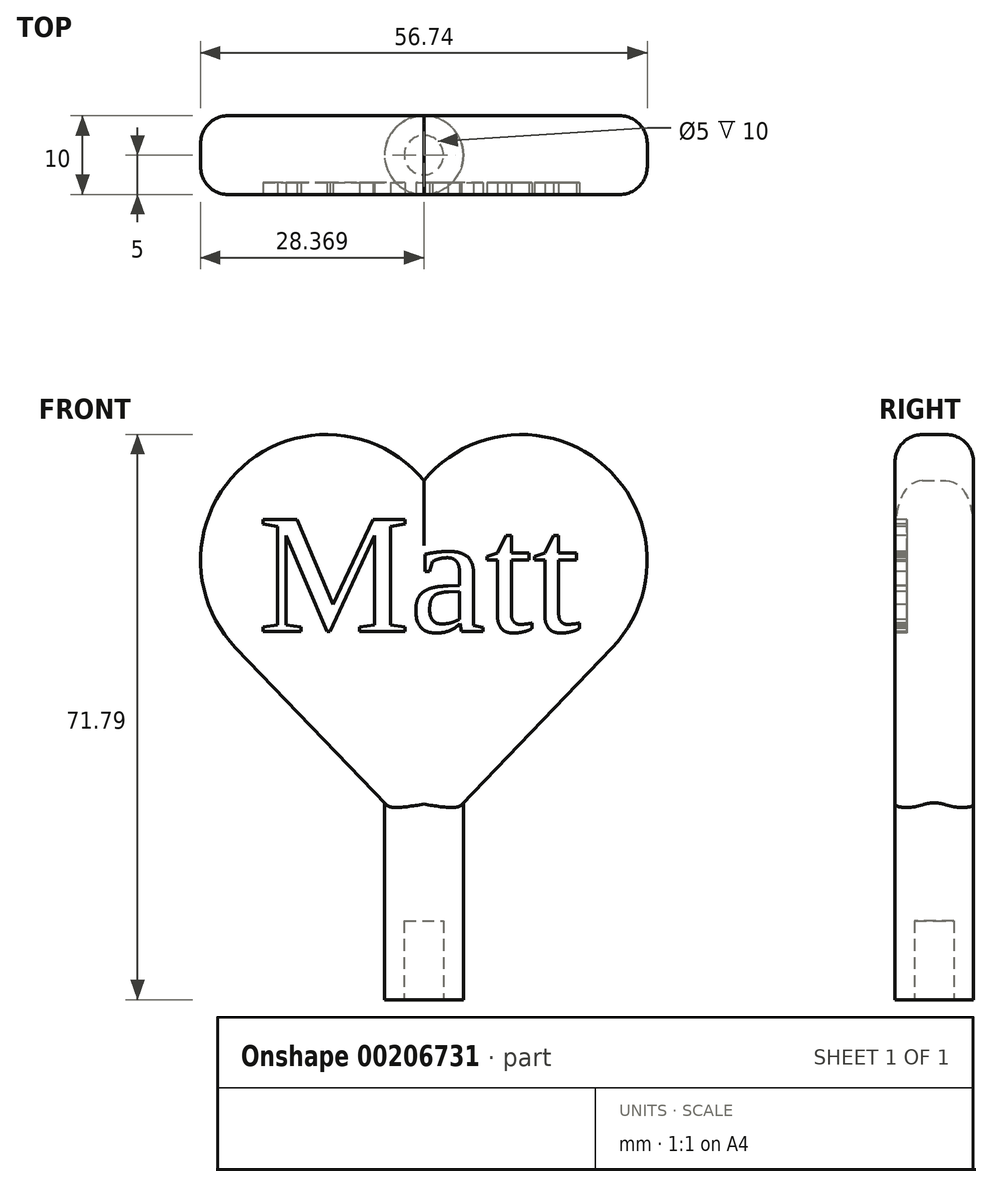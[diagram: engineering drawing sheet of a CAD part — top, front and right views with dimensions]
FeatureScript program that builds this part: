
annotation { "Feature Type Name" : "Feature", "Feature Type Description" : "" }
export const myFeature = defineFeature(function(context is Context, id is Id, definition is map)
    precondition{}
    {
        {
            var Q0;
            Q0=qCreatedBy(makeId("Front.planeOp"),FACE);
            var sketch = newSketch(context, id + "F0", { "sketchPlane" : qUnion([Q0])});
            skArc(sketch, "E0", {"start": v(-13.24, 54.95) * mm, "mid": v(-36.24, 56.75) * mm, "end": v(-37.15, 33.7) * mm});
            skArc(sketch, "E1.MirrorCS", {"start": v(-13.24, 54.95) * mm, "mid": v(9.76, 56.75) * mm, "end": v(10.67, 33.7) * mm});
            skLineSegment(sketch, "E2", {"start": v(-18.24, 14) * mm, "end": v(-8.24, 14) * mm});
            skLineSegment(sketch, "E3", {"start": v(-37.15, 33.7) * mm, "end": v(-18.24, 14) * mm});
            skLineSegment(sketch, "E4", {"start": v(10.67, 33.7) * mm, "end": v(-8.24, 14) * mm});
            skSolve(sketch);
        }
        {
            var Q0;
            Q0=makeQuery(id+"F0.imprint","IMPRINT",FACE,{"disambiguationData":[TD([[makeQuery(id+"F0.imprint","IMPRINT",EDGE,{"derivedFrom":sQuery(id+"F0.wireOp",EDGE,"E0")}),1.0]])]});
            extrude(context, id + "F1", {"entities" : qUnion([Q0]), "depth" : 10 * mm});
        }
        {
            var Q0;
            Q0=makeQuery(id+"F1.opExtrude","SWEPT_FACE",FACE,{"disambiguationData":[OSD([sQuery(id+"F0.wireOp",EDGE,"E2")])]});
            extrude(context, id + "F2", {"entities" : qUnion([Q0]), "operationType" : NewBodyOperationType.ADD, "depth" : 25 * mm});
        }
        {
            var Q0;
            Q0=makeQuery(id+"F1.opExtrude","CAP_EDGE",EDGE,{"disambiguationData":[OSD([sQuery(id+"F0.wireOp",EDGE,"E1.MirrorCS")])],"isStart":false});
            var Q1;
            Q1=makeQuery(id+"F1.opExtrude","CAP_EDGE",EDGE,{"disambiguationData":[OSD([sQuery(id+"F0.wireOp",EDGE,"E0")])],"isStart":false});
            var Q2;
            Q2=makeQuery(id+"F1.opExtrude","CAP_EDGE",EDGE,{"disambiguationData":[OSD([sQuery(id+"F0.wireOp",EDGE,"E3")])],"isStart":false});
            var Q3;
            Q3=makeQuery(id+"F1.opExtrude","CAP_EDGE",EDGE,{"disambiguationData":[OSD([sQuery(id+"F0.wireOp",EDGE,"E4")])],"isStart":false});
            var Q4;
            Q4=makeQuery(id+"F1.opExtrude","CAP_EDGE",EDGE,{"disambiguationData":[OSD([sQuery(id+"F0.wireOp",EDGE,"E4")])],"isStart":true});
            var Q5;
            Q5=makeQuery(id+"F1.opExtrude","CAP_EDGE",EDGE,{"disambiguationData":[OSD([sQuery(id+"F0.wireOp",EDGE,"E1.MirrorCS")])],"isStart":true});
            var Q6;
            Q6=makeQuery(id+"F1.opExtrude","CAP_EDGE",EDGE,{"disambiguationData":[OSD([sQuery(id+"F0.wireOp",EDGE,"E0")])],"isStart":true});
            var Q7;
            Q7=makeQuery(id+"F1.opExtrude","CAP_EDGE",EDGE,{"disambiguationData":[OSD([sQuery(id+"F0.wireOp",EDGE,"E3")])],"isStart":true});
            fillet(context, id + "F3", {"entities" : qUnion([Q0, Q1, Q2, Q3, Q4, Q5, Q6, Q7]), "radius" : 3.5 * mm, "tangentPropagation" : true, "allowEdgeOverflow" : false});
        }
        {
            var Q0;
            {var subQ0=sQuery(id+"F0.wireOp",EDGE,"E3");var subQ1=sQuery(id+"F0.wireOp",EDGE,"E2");Q0=makeQuery(id+"F2.opExtrude","SWEPT_EDGE",EDGE,{"disambiguationData":[OSD([subQ1,subQ0]),TDD([makeQuery(id+"F1.opExtrude","CAP_VERTEX",VERTEX,{"disambiguationData":[OSD([subQ1,subQ0])],"isStart":false})])]});}
            var Q1;
            {var subQ0=sQuery(id+"F0.wireOp",EDGE,"E4");var subQ1=sQuery(id+"F0.wireOp",EDGE,"E2");Q1=makeQuery(id+"F2.opExtrude","SWEPT_EDGE",EDGE,{"disambiguationData":[OSD([subQ1,subQ0]),TDD([makeQuery(id+"F1.opExtrude","CAP_VERTEX",VERTEX,{"disambiguationData":[OSD([subQ1,subQ0])],"isStart":false})])]});}
            var Q2;
            {var subQ0=sQuery(id+"F0.wireOp",EDGE,"E4");var subQ1=sQuery(id+"F0.wireOp",EDGE,"E2");Q2=makeQuery(id+"F2.opExtrude","SWEPT_EDGE",EDGE,{"disambiguationData":[OSD([subQ1,subQ0]),TDD([makeQuery(id+"F1.opExtrude","CAP_VERTEX",VERTEX,{"disambiguationData":[OSD([subQ1,subQ0])],"isStart":true})])]});}
            var Q3;
            {var subQ0=sQuery(id+"F0.wireOp",EDGE,"E3");var subQ1=sQuery(id+"F0.wireOp",EDGE,"E2");Q3=makeQuery(id+"F2.opExtrude","SWEPT_EDGE",EDGE,{"disambiguationData":[OSD([subQ1,subQ0]),TDD([makeQuery(id+"F1.opExtrude","CAP_VERTEX",VERTEX,{"disambiguationData":[OSD([subQ1,subQ0])],"isStart":true})])]});}
            fillet(context, id + "F4", {"entities" : qUnion([Q0, Q1, Q2, Q3]), "radius" : 5 * mm, "tangentPropagation" : true, "allowEdgeOverflow" : false});
        }
        {
            var Q0;
            Q0=makeQuery(id+"F2.opExtrude","CAP_FACE",FACE,{"disambiguationData":[OSD([sQuery(id+"F0.wireOp",EDGE,"E2")])],"isStart":false});
            var sketch = newSketch(context, id + "F5", { "sketchPlane" : qUnion([Q0])});
            skCircle(sketch, "E5", {"center": v(-13.24, 5) * mm, "radius": 2.5 * mm});
            skSolve(sketch);
        }
        {
            var Q0;
            {var subQ0=sQuery(id+"F0.wireOp",EDGE,"E2");Q0=makeQuery(id+"F2.boolean.opBoolean","MERGE",FACE,{"derivedFrom":[makeQuery(id+"F1.opExtrude","CAP_FACE",FACE,{"disambiguationData":[OSD([sQuery(id+"F0.wireOp",EDGE,"E0"),sQuery(id+"F0.wireOp",EDGE,"E1.MirrorCS"),subQ0,sQuery(id+"F0.wireOp",EDGE,"E3"),sQuery(id+"F0.wireOp",EDGE,"E4")])],"isStart":false}),makeQuery(id+"F2.opExtrude","SWEPT_FACE",FACE,{"disambiguationData":[OSD([subQ0]),TDD([makeQuery(id+"F1.opExtrude","CAP_EDGE",EDGE,{"disambiguationData":[OSD([subQ0])],"isStart":false})])]})]});}
            var sketch = newSketch(context, id + "F6", { "sketchPlane" : qUnion([Q0])});
            skText(sketch, "E6", { "text": "Matt", "fontName": "Tinos-Regular.ttf"});
            const initialGuessF6  = {"E6": [-0.0343, 0.03578, 1, 0, 0.0156]};
            skSetInitialGuess(sketch, initialGuessF6);
            skSolve(sketch);
        }
        {
            var Q0;
            Q0=makeQuery(id+"F6.imprint","IMPRINT",FACE,{"disambiguationData":[TD([[makeQuery(id+"F6.imprint","IMPRINT",EDGE,{"derivedFrom":sQuery(id+"F6.wireOp",EDGE,"E6.sketch_text.stroke-0")}),-1.0]])]});
            var Q1;
            Q1=makeQuery(id+"F6.imprint","IMPRINT",FACE,{"disambiguationData":[TD([[makeQuery(id+"F6.imprint","IMPRINT",EDGE,{"derivedFrom":sQuery(id+"F6.wireOp",EDGE,"E6.sketch_text.stroke-25")}),-1.0]])]});
            var Q2;
            Q2=makeQuery(id+"F6.imprint","IMPRINT",FACE,{"disambiguationData":[TD([[makeQuery(id+"F6.imprint","IMPRINT",EDGE,{"derivedFrom":sQuery(id+"F6.wireOp",EDGE,"E6.sketch_text.stroke-53")}),-1.0]])]});
            var Q3;
            Q3=makeQuery(id+"F6.imprint","IMPRINT",FACE,{"disambiguationData":[TD([[makeQuery(id+"F6.imprint","IMPRINT",EDGE,{"derivedFrom":sQuery(id+"F6.wireOp",EDGE,"E6.sketch_text.stroke-72")}),-1.0]])]});
            extrude(context, id + "F7", {"entities" : qUnion([Q0, Q1, Q2, Q3]), "operationType" : NewBodyOperationType.REMOVE, "oppositeDirection" : true, "depth" : 1.5 * mm});
        }
        {
            var Q0;
            Q0=makeQuery(id+"F5.imprint","IMPRINT",FACE,{"disambiguationData":[TD([[makeQuery(id+"F5.imprint","IMPRINT",EDGE,{"derivedFrom":sQuery(id+"F5.wireOp",EDGE,"E5")}),1.0]])]});
            extrude(context, id + "F8", {"entities" : qUnion([Q0]), "operationType" : NewBodyOperationType.REMOVE, "oppositeDirection" : true, "depth" : 10 * mm});
        }
    });
